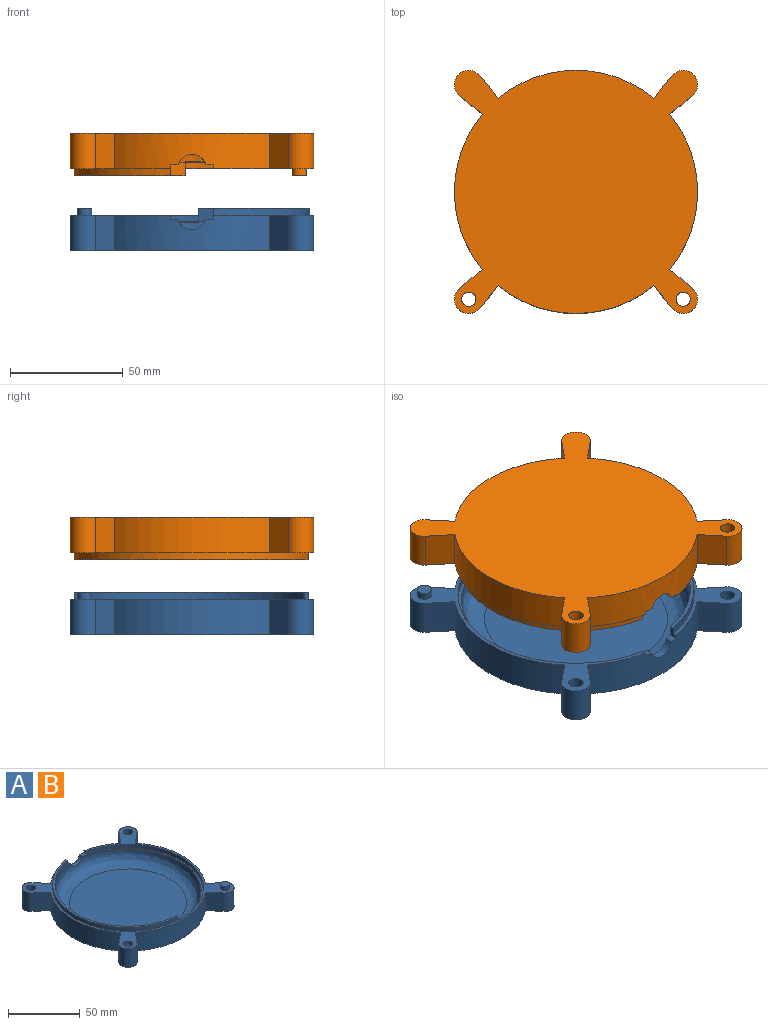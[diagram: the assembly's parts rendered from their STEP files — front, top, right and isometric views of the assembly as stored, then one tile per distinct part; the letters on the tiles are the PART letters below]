
ASSEMBLY  parts=2 mates=1
PART A: 40 faces, bbox 108x108x18.9 mm
  f0: plane 107.95x107.95mm, normal (0,0,-1), area 9960mm2, adj f18,f19,f24,f25,f26,f27,f28,f29
  f1: plane 3.72x3.38mm, normal (0,0,1), area 10.8mm2, adj f3,f5,f7,f16,f31
  f2: plane 3.72x3.38mm, normal (0,0,1), area 10.8mm2, adj f6,f7,f8,f31
  f3: cylinder r=50.8mm len=3.71mm, axis (0,0,-1), area 3.4mm2, adj f1,f7,f10,f16
  f4: plane 107.95x107.95mm, normal (0,0,1), area 1242mm2, adj f5,f6,f11,f14,f15,f18,f19,f20
  f5: plane 1.6x1.59mm, normal (-1,0,0), area 2.5mm2, adj f1,f4,f15,f31
  f6: plane 4.76x3.23mm, normal (1,0,0), area 10.3mm2, adj f2,f4,f8,f11,f12,f31
  f7: cylinder r=6.35mm len=12.3mm, axis (0,-1,0), area 52.9mm2, adj f1,f2,f3,f8,f10,f31
  f8: cylinder r=50.8mm len=101.17mm, axis (0,0,-1), area 843.1mm2, adj f2,f6,f7,f10,f12,f14
  f9: plane 81.3x81.3mm, normal (0,0,1), area 5187.9mm2, adj f10
  f10: bspline ~101.6x101.6mm, area 4872mm2, adj f3,f7,f8,f9,f13
  f11: cylinder r=52.39mm len=103.81mm, axis (0,0,-1), area 482.1mm2, adj f4,f6,f12,f14
  f12: plane 103.81x49.31mm, normal (0,0,1), area 237.1mm2, adj f6,f8,f11,f14
  f13: cylinder r=50.8mm len=100.7mm, axis (0,0,1), area 101.1mm2, adj f10,f14,f16,f17
  f14: plane 6.38x1.6mm, normal (1,-0.06,0), area 10.2mm2, adj f4,f8,f11,f12,f13,f15,f17
  f15: cylinder r=52.4mm len=103.93mm, axis (0,0,1), area 506.4mm2, adj f4,f5,f14,f16,f17
  f16: plane 1.63x1.61mm, normal (1,0,0), area 2.6mm2, adj f1,f3,f13,f15,f17
  f17: plane 103.93x55.57mm, normal (0,0,1), area 249.1mm2, adj f13,f14,f15,f16
  f18: cylinder r=3.19mm len=15.71mm, axis (0,0,1), area 314.7mm2, adj f0,f4
  f19: cylinder r=3.19mm len=15.71mm, axis (0,0,1), area 314.7mm2, adj f0,f4
  f20: cylinder r=3.19mm len=6.38mm, axis (0,0,1), area 64.1mm2, adj f4,f21
  f21: plane 6.38x6.38mm, normal (0,0,1), area 31.9mm2, adj f20
  f22: cylinder r=3.17mm len=6.35mm, axis (0,0,-1), area 63.3mm2, adj f4,f23
  f23: plane 6.35x6.35mm, normal (0,0,1), area 31.7mm2, adj f22
  f24: cylinder r=53.98mm len=68.8mm, axis (0,0,1), area 1171.8mm2, adj f0,f4,f32,f33
  f25: cylinder r=6.35mm len=15.71mm, axis (0,0,1), area 332.2mm2, adj f0,f4,f33,f34
  f26: cylinder r=53.98mm len=68.8mm, axis (0,0,1), area 1171.8mm2, adj f0,f4,f34,f35
  f27: cylinder r=6.35mm len=15.71mm, axis (0,0,1), area 332.2mm2, adj f0,f4,f35,f36
  f28: cylinder r=53.98mm len=68.8mm, axis (0,0,1), area 1171.8mm2, adj f0,f4,f36,f37
  f29: cylinder r=6.35mm len=15.71mm, axis (0,0,1), area 332.2mm2, adj f0,f4,f37,f38
  f30: cylinder r=6.35mm len=15.71mm, axis (0,0,1), area 332.2mm2, adj f0,f4,f32,f39
  f31: cylinder r=53.98mm len=68.8mm, axis (0,0,1), area 1098mm2, adj f0,f1,f2,f4,f5,f6,f7,f38
  f32: plane 15.71x10.08mm, normal (-0.64,-0.77,0), area 205.4mm2, adj f0,f4,f24,f30
  f33: plane 15.71x10.08mm, normal (-0.64,0.77,0), area 205.4mm2, adj f0,f4,f24,f25
  f34: plane 15.71x10.08mm, normal (0.77,-0.64,0), area 205.4mm2, adj f0,f4,f25,f26
  f35: plane 15.71x10.08mm, normal (-0.77,-0.64,0), area 205.4mm2, adj f0,f4,f26,f27
  f36: plane 15.71x10.08mm, normal (0.64,0.77,0), area 205.4mm2, adj f0,f4,f27,f28
  f37: plane 15.71x10.08mm, normal (0.64,-0.77,0), area 205.4mm2, adj f0,f4,f28,f29
  f38: plane 15.71x10.08mm, normal (-0.77,0.64,0), area 205.4mm2, adj f0,f4,f29,f31
  f39: plane 15.71x10.08mm, normal (0.77,0.64,0), area 205.4mm2, adj f0,f4,f30,f31
PART B: same geometry as A
PLACE A rot(axis=(0,0,1),180deg) t=(-0.6,-16.11,-9.32)mm
PLACE B rot(axis=(-1,0,0),180deg) t=(-0.6,-16.11,11.52)mm
MATE slider B.f19 <-> A.f18  axis (0,0,-1) through (-48.23,-63.74,11.52)mm
